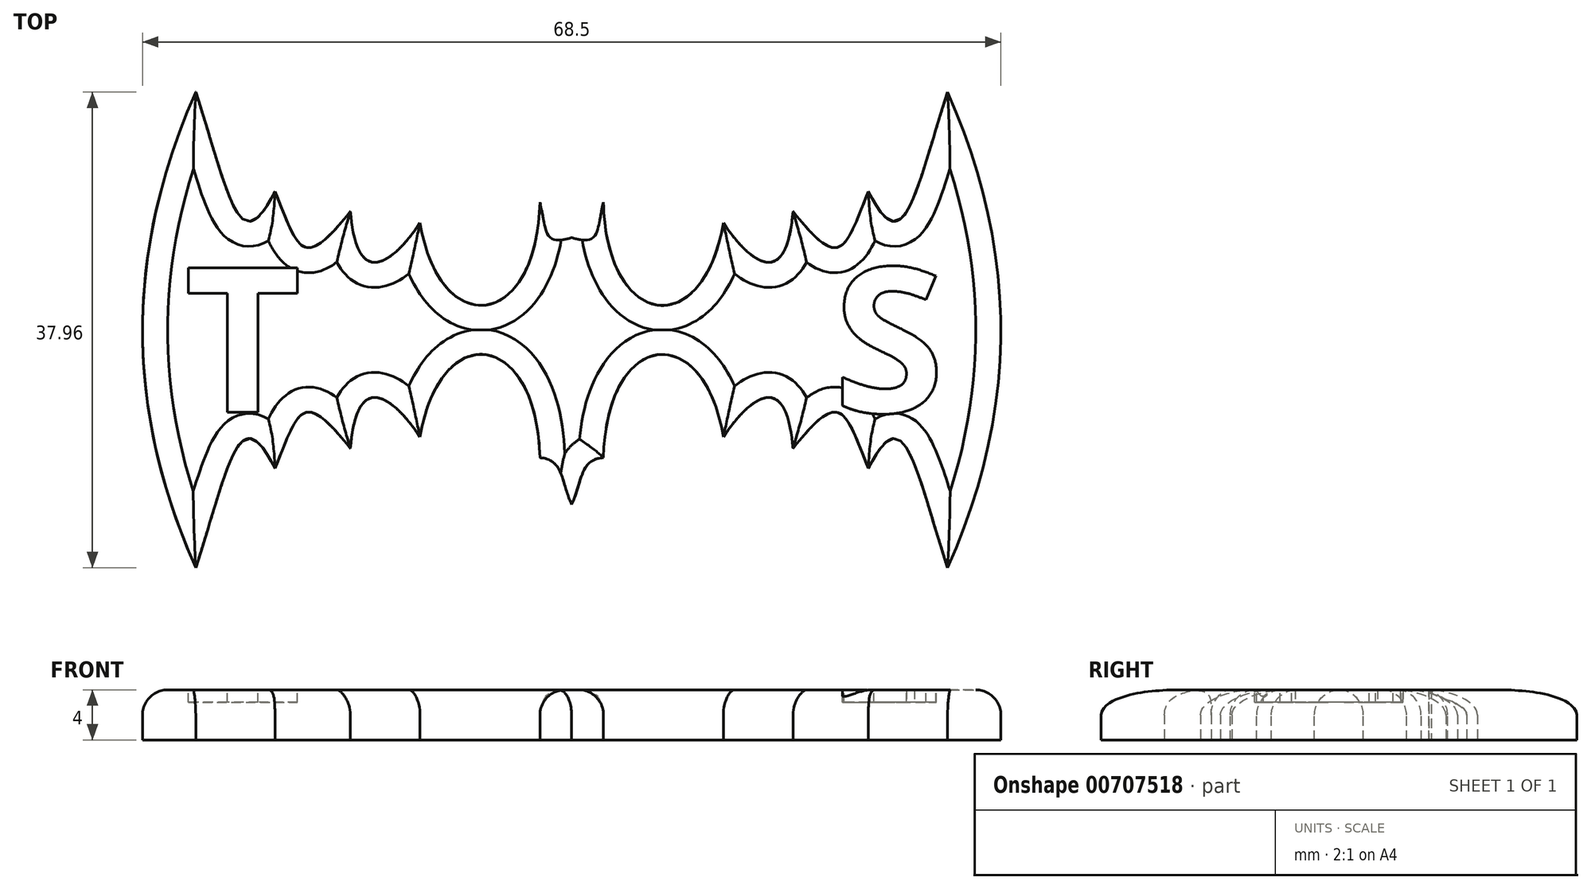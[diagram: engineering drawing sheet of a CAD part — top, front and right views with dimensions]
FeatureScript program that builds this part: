
annotation { "Feature Type Name" : "Feature", "Feature Type Description" : "" }
export const myFeature = defineFeature(function(context is Context, id is Id, definition is map)
    precondition{}
    {
        {
            var Q0;
            Q0=qCreatedBy(makeId("Top.planeOp"),FACE);
            var sketch = newSketch(context, id + "F0", { "sketchPlane" : qUnion([Q0])});
            skFitSpline(sketch, "E0", {"points": [v(-30, 18.98) * mm, v(-30, -18.98) * mm], "startDerivative": vector(-17.28, -39.16) * mm, "endDerivative": vector(16.7, -37.44) * mm});
            skFitSpline(sketch, "E1", {"points": [v(-30, 18.98) * mm, v(-23.68, 11.06) * mm], "startDerivative": vector(8.06, -24.76) * mm, "endDerivative": vector(8.64, 17.28) * mm});
            skFitSpline(sketch, "E2", {"points": [v(-23.68, 11.06) * mm, v(-17.66, 9.46) * mm], "startDerivative": vector(5.76, -14.4) * mm, "endDerivative": vector(11.52, 14.4) * mm});
            skFitSpline(sketch, "E3", {"points": [v(-17.66, 9.46) * mm, v(-12.1, 8.54) * mm], "startDerivative": vector(1.73, -21.3) * mm, "endDerivative": vector(4.6, 6.91) * mm});
            skFitSpline(sketch, "E4", {"points": [v(-12.1, 8.54) * mm, v(-2.53, 10.2) * mm], "startDerivative": vector(4.8, -28.5) * mm, "endDerivative": vector(0.72, 30.62) * mm});
            skFitSpline(sketch, "E5", {"points": [v(-2.53, 10.2) * mm, v(0, 7.36) * mm], "startDerivative": vector(1.7, -7.76) * mm, "endDerivative": vector(6.58, 1.95) * mm});
            skFitSpline(sketch, "E6.MirrorCS", {"points": [v(-30, -18.98) * mm, v(-23.68, -11.06) * mm], "startDerivative": vector(8.06, 24.76) * mm, "endDerivative": vector(8.64, -17.28) * mm});
            skFitSpline(sketch, "E7.MirrorCS", {"points": [v(-17.66, -9.46) * mm, v(-12.1, -8.54) * mm], "startDerivative": vector(1.73, 21.3) * mm, "endDerivative": vector(4.6, -6.91) * mm});
            skFitSpline(sketch, "E8.MirrorCS", {"points": [v(-23.68, -11.06) * mm, v(-17.66, -9.46) * mm], "startDerivative": vector(5.76, 14.4) * mm, "endDerivative": vector(11.52, -14.4) * mm});
            skFitSpline(sketch, "E9.MirrorCS", {"points": [v(-12.1, -8.54) * mm, v(-2.53, -10.2) * mm], "startDerivative": vector(4.8, 28.5) * mm, "endDerivative": vector(0.72, -30.62) * mm});
            skFitSpline(sketch, "E10", {"points": [v(-2.53, -10.2) * mm, v(0, -13.93) * mm], "startDerivative": vector(5.71, -0.23) * mm, "endDerivative": vector(2.46, -5.03) * mm});
            skFitSpline(sketch, "E11.MirrorCS", {"points": [v(2.53, -10.2) * mm, v(0, -13.93) * mm], "startDerivative": vector(-5.71, -0.23) * mm, "endDerivative": vector(-2.46, -5.03) * mm});
            skFitSpline(sketch, "E12.MirrorCS", {"points": [v(2.53, 10.2) * mm, v(0, 7.36) * mm], "startDerivative": vector(-1.7, -7.76) * mm, "endDerivative": vector(-6.58, 1.95) * mm});
            skFitSpline(sketch, "E13.MirrorCS", {"points": [v(12.1, -8.54) * mm, v(2.53, -10.2) * mm], "startDerivative": vector(-4.8, 28.5) * mm, "endDerivative": vector(-0.72, -30.62) * mm});
            skFitSpline(sketch, "E14.MirrorCS", {"points": [v(12.1, 8.54) * mm, v(2.53, 10.2) * mm], "startDerivative": vector(-4.8, -28.5) * mm, "endDerivative": vector(-0.72, 30.62) * mm});
            skFitSpline(sketch, "E15.MirrorCS", {"points": [v(17.66, 9.46) * mm, v(12.1, 8.54) * mm], "startDerivative": vector(-1.73, -21.3) * mm, "endDerivative": vector(-4.6, 6.91) * mm});
            skFitSpline(sketch, "E16.MirrorCS", {"points": [v(23.68, 11.06) * mm, v(17.66, 9.46) * mm], "startDerivative": vector(-5.76, -14.4) * mm, "endDerivative": vector(-11.52, 14.4) * mm});
            skFitSpline(sketch, "E17.MirrorCS", {"points": [v(23.68, -11.06) * mm, v(17.66, -9.46) * mm], "startDerivative": vector(-5.76, 14.4) * mm, "endDerivative": vector(-11.52, -14.4) * mm});
            skFitSpline(sketch, "E18.MirrorCS", {"points": [v(17.66, -9.46) * mm, v(12.1, -8.54) * mm], "startDerivative": vector(-1.73, 21.3) * mm, "endDerivative": vector(-4.6, -6.91) * mm});
            skFitSpline(sketch, "E19.MirrorCS", {"points": [v(30, 18.98) * mm, v(23.68, 11.06) * mm], "startDerivative": vector(-8.06, -24.76) * mm, "endDerivative": vector(-8.64, 17.28) * mm});
            skFitSpline(sketch, "E20.MirrorCS", {"points": [v(30, 18.98) * mm, v(30, -18.98) * mm], "startDerivative": vector(17.28, -39.16) * mm, "endDerivative": vector(-16.7, -37.44) * mm});
            skFitSpline(sketch, "E21.MirrorCS", {"points": [v(30, -18.98) * mm, v(23.68, -11.06) * mm], "startDerivative": vector(-8.06, 24.76) * mm, "endDerivative": vector(-8.64, -17.28) * mm});
            skSolve(sketch);
        }
        {
            var Q0;
            Q0=makeQuery(id+"F0.imprint","IMPRINT",FACE,{"disambiguationData":[TD([[makeQuery(id+"F0.imprint","IMPRINT",EDGE,{"derivedFrom":sQuery(id+"F0.wireOp",EDGE,"E0")}),1.0]])]});
            extrude(context, id + "F1", {"entities" : qUnion([Q0]), "depth" : 4 * mm, "offsetDistance" : 25 * mm});
        }
        {
            var Q0;
            Q0=makeQuery(id+"F1.opExtrude","CAP_FACE",FACE,{"disambiguationData":[OSD([sQuery(id+"F0.wireOp",EDGE,"E0"),sQuery(id+"F0.wireOp",EDGE,"E1"),sQuery(id+"F0.wireOp",EDGE,"E2"),sQuery(id+"F0.wireOp",EDGE,"E3"),sQuery(id+"F0.wireOp",EDGE,"E4"),sQuery(id+"F0.wireOp",EDGE,"E5"),sQuery(id+"F0.wireOp",EDGE,"E6.MirrorCS"),sQuery(id+"F0.wireOp",EDGE,"E7.MirrorCS"),sQuery(id+"F0.wireOp",EDGE,"E8.MirrorCS"),sQuery(id+"F0.wireOp",EDGE,"E9.MirrorCS"),sQuery(id+"F0.wireOp",EDGE,"E10"),sQuery(id+"F0.wireOp",EDGE,"E11.MirrorCS"),sQuery(id+"F0.wireOp",EDGE,"E12.MirrorCS"),sQuery(id+"F0.wireOp",EDGE,"E13.MirrorCS"),sQuery(id+"F0.wireOp",EDGE,"E14.MirrorCS"),sQuery(id+"F0.wireOp",EDGE,"E15.MirrorCS"),sQuery(id+"F0.wireOp",EDGE,"E16.MirrorCS"),sQuery(id+"F0.wireOp",EDGE,"E17.MirrorCS"),sQuery(id+"F0.wireOp",EDGE,"E18.MirrorCS"),sQuery(id+"F0.wireOp",EDGE,"E19.MirrorCS"),sQuery(id+"F0.wireOp",EDGE,"E20.MirrorCS"),sQuery(id+"F0.wireOp",EDGE,"E21.MirrorCS")])],"isStart":false});
            var sketch = newSketch(context, id + "F2", { "sketchPlane" : qUnion([Q0])});
            skText(sketch, "E22", { "text": "T", "fontName": "OpenSans-Bold.ttf"});
            skText(sketch, "E23", { "text": "S", "fontName": "OpenSans-Bold.ttf"});
            const initialGuessF2  = {"E22": [-0.03092, -0.00657, 1, 0, 0.01162], "E23": [0.02086, -0.00657, 1, 0, 0.01162]};
            skSetInitialGuess(sketch, initialGuessF2);
            skSolve(sketch);
        }
        {
            var Q0;
            Q0 = qSketchRegion(id + "F2", true);
            extrude(context, id + "F3", {"entities" : qUnion([Q0]), "operationType" : NewBodyOperationType.REMOVE, "oppositeDirection" : true, "depth" : 1 * mm, "offsetDistance" : 25 * mm});
        }
        {
            var Q0;
            Q0=makeQuery(id+"F1.opExtrude","CAP_EDGE",EDGE,{"disambiguationData":[OSD([sQuery(id+"F0.wireOp",EDGE,"E0")])],"isStart":false});
            var Q1;
            Q1=makeQuery(id+"F1.opExtrude","CAP_EDGE",EDGE,{"disambiguationData":[OSD([sQuery(id+"F0.wireOp",EDGE,"E1")])],"isStart":false});
            var Q2;
            Q2=makeQuery(id+"F1.opExtrude","CAP_EDGE",EDGE,{"disambiguationData":[OSD([sQuery(id+"F0.wireOp",EDGE,"E2")])],"isStart":false});
            var Q3;
            Q3=makeQuery(id+"F1.opExtrude","CAP_EDGE",EDGE,{"disambiguationData":[OSD([sQuery(id+"F0.wireOp",EDGE,"E3")])],"isStart":false});
            var Q4;
            Q4=makeQuery(id+"F1.opExtrude","CAP_EDGE",EDGE,{"disambiguationData":[OSD([sQuery(id+"F0.wireOp",EDGE,"E4")])],"isStart":false});
            var Q5;
            Q5=makeQuery(id+"F1.opExtrude","CAP_EDGE",EDGE,{"disambiguationData":[OSD([sQuery(id+"F0.wireOp",EDGE,"E14.MirrorCS")])],"isStart":false});
            var Q6;
            Q6=makeQuery(id+"F1.opExtrude","CAP_EDGE",EDGE,{"disambiguationData":[OSD([sQuery(id+"F0.wireOp",EDGE,"E15.MirrorCS")])],"isStart":false});
            var Q7;
            Q7=makeQuery(id+"F1.opExtrude","CAP_EDGE",EDGE,{"disambiguationData":[OSD([sQuery(id+"F0.wireOp",EDGE,"E16.MirrorCS")])],"isStart":false});
            var Q8;
            Q8=makeQuery(id+"F1.opExtrude","CAP_EDGE",EDGE,{"disambiguationData":[OSD([sQuery(id+"F0.wireOp",EDGE,"E19.MirrorCS")])],"isStart":false});
            var Q9;
            Q9=makeQuery(id+"F1.opExtrude","CAP_EDGE",EDGE,{"disambiguationData":[OSD([sQuery(id+"F0.wireOp",EDGE,"E20.MirrorCS")])],"isStart":false});
            var Q10;
            Q10=makeQuery(id+"F1.opExtrude","CAP_EDGE",EDGE,{"disambiguationData":[OSD([sQuery(id+"F0.wireOp",EDGE,"E21.MirrorCS")])],"isStart":false});
            var Q11;
            Q11=makeQuery(id+"F1.opExtrude","CAP_EDGE",EDGE,{"disambiguationData":[OSD([sQuery(id+"F0.wireOp",EDGE,"E17.MirrorCS")])],"isStart":false});
            var Q12;
            Q12=makeQuery(id+"F1.opExtrude","CAP_EDGE",EDGE,{"disambiguationData":[OSD([sQuery(id+"F0.wireOp",EDGE,"E18.MirrorCS")])],"isStart":false});
            var Q13;
            Q13=makeQuery(id+"F1.opExtrude","CAP_EDGE",EDGE,{"disambiguationData":[OSD([sQuery(id+"F0.wireOp",EDGE,"E13.MirrorCS")])],"isStart":false});
            var Q14;
            Q14=makeQuery(id+"F1.opExtrude","CAP_EDGE",EDGE,{"disambiguationData":[OSD([sQuery(id+"F0.wireOp",EDGE,"E11.MirrorCS")])],"isStart":false});
            var Q15;
            Q15=makeQuery(id+"F1.opExtrude","CAP_EDGE",EDGE,{"disambiguationData":[OSD([sQuery(id+"F0.wireOp",EDGE,"E9.MirrorCS")])],"isStart":false});
            var Q16;
            Q16=makeQuery(id+"F1.opExtrude","CAP_EDGE",EDGE,{"disambiguationData":[OSD([sQuery(id+"F0.wireOp",EDGE,"E7.MirrorCS")])],"isStart":false});
            var Q17;
            Q17=makeQuery(id+"F1.opExtrude","CAP_EDGE",EDGE,{"disambiguationData":[OSD([sQuery(id+"F0.wireOp",EDGE,"E8.MirrorCS")])],"isStart":false});
            var Q18;
            Q18=makeQuery(id+"F1.opExtrude","CAP_EDGE",EDGE,{"disambiguationData":[OSD([sQuery(id+"F0.wireOp",EDGE,"E6.MirrorCS")])],"isStart":false});
            fillet(context, id + "F4", {"entities" : qUnion([Q0, Q1, Q2, Q3, Q4, Q5, Q6, Q7, Q8, Q9, Q10, Q11, Q12, Q13, Q14, Q15, Q16, Q17, Q18]), "radius" : 2 * mm, "tangentPropagation" : true, "allowEdgeOverflow" : false});
        }
    });
